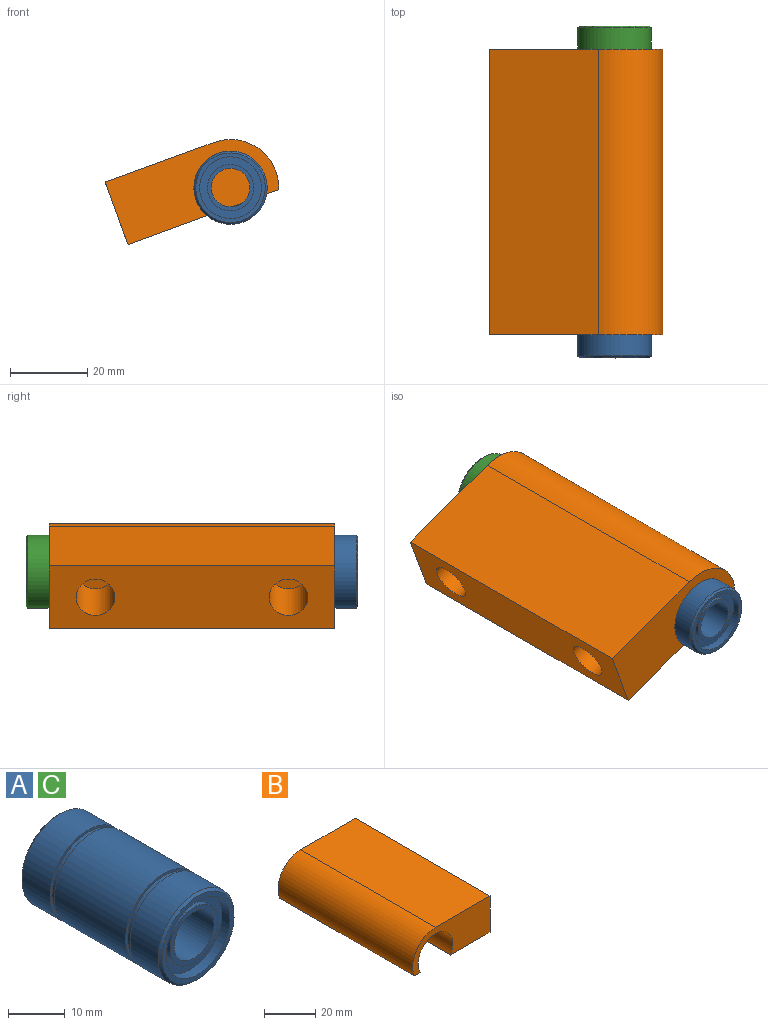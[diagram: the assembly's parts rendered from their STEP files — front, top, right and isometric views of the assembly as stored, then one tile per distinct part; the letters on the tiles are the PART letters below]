
ASSEMBLY  parts=3 mates=1
PART A: 22 faces, bbox 19x35x19 mm
  f0: plane 18x18mm, normal (0,-1,0), area 53.4mm2, adj f1,f21
  f1: cylinder r=8mm len=16mm, axis (0,1,0), area 100.5mm2, adj f0,f2
  f2: plane 16x16mm, normal (0,-1,0), area 88mm2, adj f1,f3
  f3: cylinder r=6mm len=12mm, axis (0,1,0), area 37.7mm2, adj f2,f4
  f4: plane 12x12mm, normal (0,-1,0), area 34.6mm2, adj f3,f5
  f5: cylinder r=5mm len=33mm, axis (0,1,0), area 1036.7mm2, adj f4,f6
  f6: plane 12x12mm, normal (0,1,0), area 34.6mm2, adj f5,f7
  f7: cylinder r=6mm len=12mm, axis (0,1,0), area 37.7mm2, adj f6,f8
  f8: plane 16x16mm, normal (0,1,0), area 88mm2, adj f7,f9
  f9: cylinder r=8mm len=16mm, axis (0,1,0), area 100.5mm2, adj f8,f10
  f10: plane 18x18mm, normal (0,1,0), area 53.4mm2, adj f9,f11
  f11: cone r=9mm half-angle=45deg, axis (0,-1,0), area 41.1mm2, adj f10,f12
  f12: cylinder r=9.5mm len=19mm, axis (0,1,0), area 417.8mm2, adj f11,f13
  f13: plane 19x19mm, normal (0,-1,0), area 29.1mm2, adj f12,f14
  f14: cylinder r=9mm len=18mm, axis (0,1,0), area 62.2mm2, adj f13,f15
  f15: plane 19x19mm, normal (0,1,0), area 29.1mm2, adj f14,f16
  f16: cylinder r=9.5mm len=19mm, axis (0,1,0), area 1062.5mm2, adj f15,f17
  f17: plane 19x19mm, normal (0,-1,0), area 29.1mm2, adj f16,f18
  f18: cylinder r=9mm len=18mm, axis (0,1,0), area 62.2mm2, adj f17,f19
  f19: plane 19x19mm, normal (0,1,0), area 29.1mm2, adj f18,f20
  f20: cylinder r=9.5mm len=19mm, axis (0,1,0), area 417.8mm2, adj f19,f21
  f21: cone r=9mm half-angle=45deg, axis (0,1,0), area 41.1mm2, adj f0,f20
PART B: 14 faces, bbox 42.5x74x17.3 mm
  f0: plane 19x14.25mm, normal (0,1,0), area 228.1mm2, adj f2,f8
  f1: plane 19x14.25mm, normal (0,-1,0), area 228.1mm2, adj f2,f6
  f2: plane 74x41.56mm, normal (0,0,-1), area 2433.9mm2, adj f0,f1,f3,f5,f6,f7,f8,f9
  f3: plane 74x17.25mm, normal (1,0,0), area 1119.4mm2, adj f2,f4,f7,f9,f10,f12
  f4: plane 74x30mm, normal (0,0,1), area 2220mm2, adj f3,f5,f7,f9
  f5: cylinder r=12.5mm len=74mm, axis (0,-1,0), area 1813.5mm2, adj f2,f4,f7,f9
  f6: cylinder r=9.5mm len=29mm, axis (0,1,0), area 1154mm2, adj f1,f2,f7
  f7: plane 42.5x17.25mm, normal (0,-1,0), area 470mm2, adj f2,f3,f4,f5,f6
  f8: cylinder r=9.5mm len=19mm, axis (0,1,0), area 397.9mm2, adj f0,f2,f9
  f9: plane 42.5x17.25mm, normal (0,1,0), area 470mm2, adj f2,f3,f4,f5,f8
  f10: cylinder r=5mm len=20mm, axis (1,0,0), area 628.3mm2, adj f3,f11
  f11: plane 10x10mm, normal (1,0,0), area 78.5mm2, adj f10
  f12: cylinder r=5mm len=20mm, axis (1,0,0), area 628.3mm2, adj f3,f13
  f13: plane 10x10mm, normal (1,0,0), area 78.5mm2, adj f12
PART C: same geometry as A
PLACE A rot(axis=(0.17,0,-0.98),180deg) t=(-11.36,-72.93,51.76)mm
PLACE B rot(axis=(0.17,0,-0.98),180deg) t=(-77.37,-39.43,12.56)mm
PLACE C rot(axis=(0.17,0,-0.98),180deg) t=(-11.36,-21.93,51.76)mm
MATE fastened B.f5 <-> C.f1  axis (0,1,0) through (-11.36,-39.43,51.76)mm
